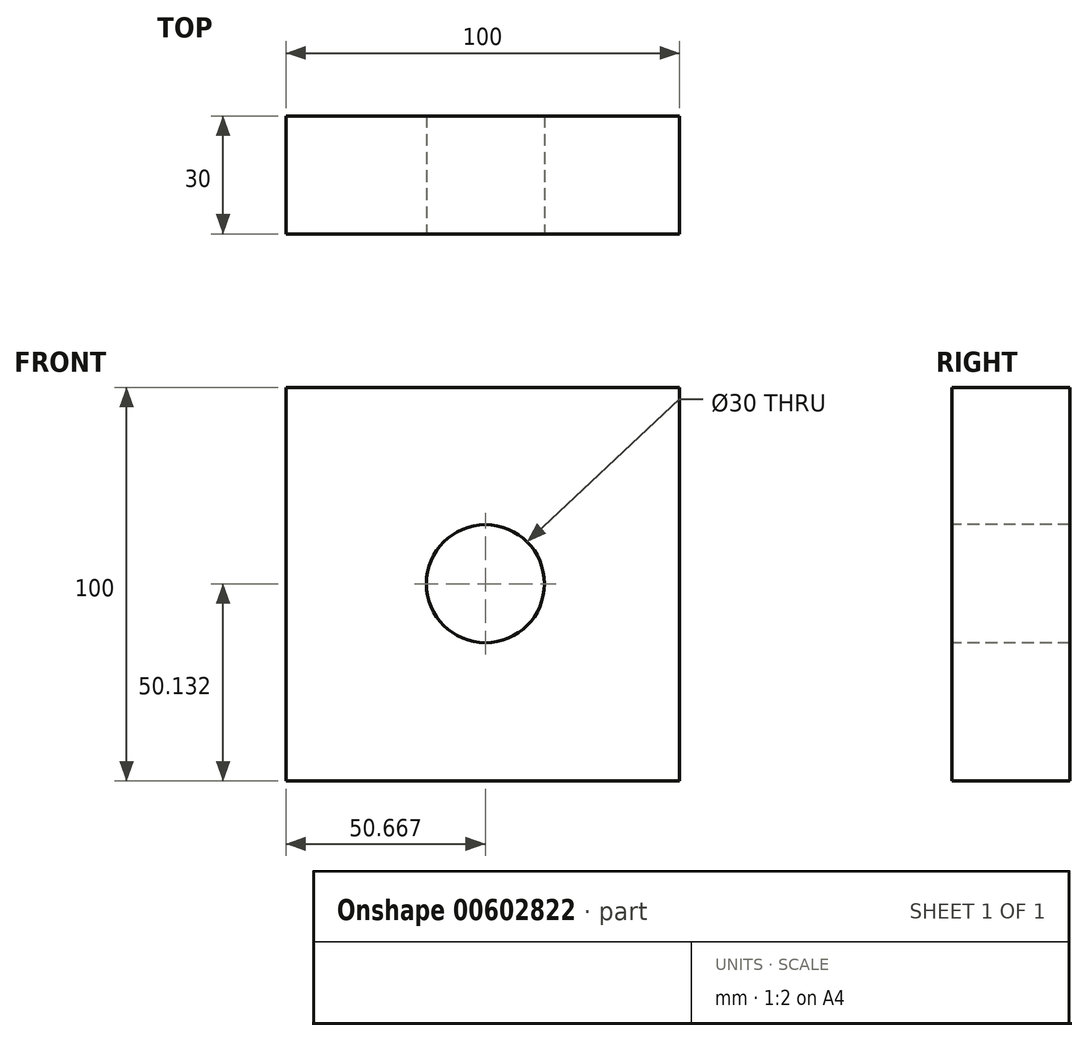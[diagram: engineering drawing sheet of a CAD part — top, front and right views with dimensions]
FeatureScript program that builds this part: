
annotation { "Feature Type Name" : "Feature", "Feature Type Description" : "" }
export const myFeature = defineFeature(function(context is Context, id is Id, definition is map)
    precondition{}
    {
        {
            var Q0;
            Q0=qCreatedBy(makeId("Front.planeOp"),FACE);
            var sketch = newSketch(context, id + "F0", { "sketchPlane" : qUnion([Q0])});
            skLineSegment(sketch, "E0.bottom", {"start": v(-100, 100) * mm, "end": v(0, 100) * mm});
            skLineSegment(sketch, "E0.top", {"start": v(-100, 0) * mm, "end": v(0, 0) * mm});
            skLineSegment(sketch, "E0.left", {"start": v(-100, 100) * mm, "end": v(-100, 0) * mm});
            skLineSegment(sketch, "E0.right", {"start": v(0, 100) * mm, "end": v(0, 0) * mm});
            skSolve(sketch);
        }
        {
            var Q0;
            Q0=makeQuery(id+"F0.imprint","IMPRINT",FACE,{"disambiguationData":[TD([[makeQuery(id+"F0.imprint","IMPRINT",EDGE,{"derivedFrom":sQuery(id+"F0.wireOp",EDGE,"E0.bottom")}),-1.0]])]});
            extrude(context, id + "F1", {"entities" : qUnion([Q0]), "oppositeDirection" : true, "depth" : 30 * mm, "offsetDistance" : 25 * mm});
        }
        {
            var Q0;
            Q0=makeQuery(id+"F1.opExtrude","CAP_FACE",FACE,{"disambiguationData":[OSD([sQuery(id+"F0.wireOp",EDGE,"E0.bottom"),sQuery(id+"F0.wireOp",EDGE,"E0.top"),sQuery(id+"F0.wireOp",EDGE,"E0.left"),sQuery(id+"F0.wireOp",EDGE,"E0.right")])],"isStart":true});
            var sketch = newSketch(context, id + "F2", { "sketchPlane" : qUnion([Q0])});
            skCircle(sketch, "E1", {"center": v(-49.33, 50.13) * mm, "radius": 15 * mm});
            skSolve(sketch);
        }
        {
            var Q0;
            Q0=makeQuery(id+"F2.imprint","IMPRINT",FACE,{"disambiguationData":[TD([[makeQuery(id+"F2.imprint","IMPRINT",EDGE,{"derivedFrom":sQuery(id+"F2.wireOp",EDGE,"E1")}),1.0]])]});
            var Q1;
            Q1=sQuery(id+"F2.wireOp",EDGE,"E1");
            extrude(context, id + "F3", {"entities" : qUnion([Q0]), "operationType" : NewBodyOperationType.REMOVE, "surfaceEntities" : qUnion([Q1]), "oppositeDirection" : true, "depth" : 50 * mm, "offsetDistance" : 25 * mm});
        }
    });
